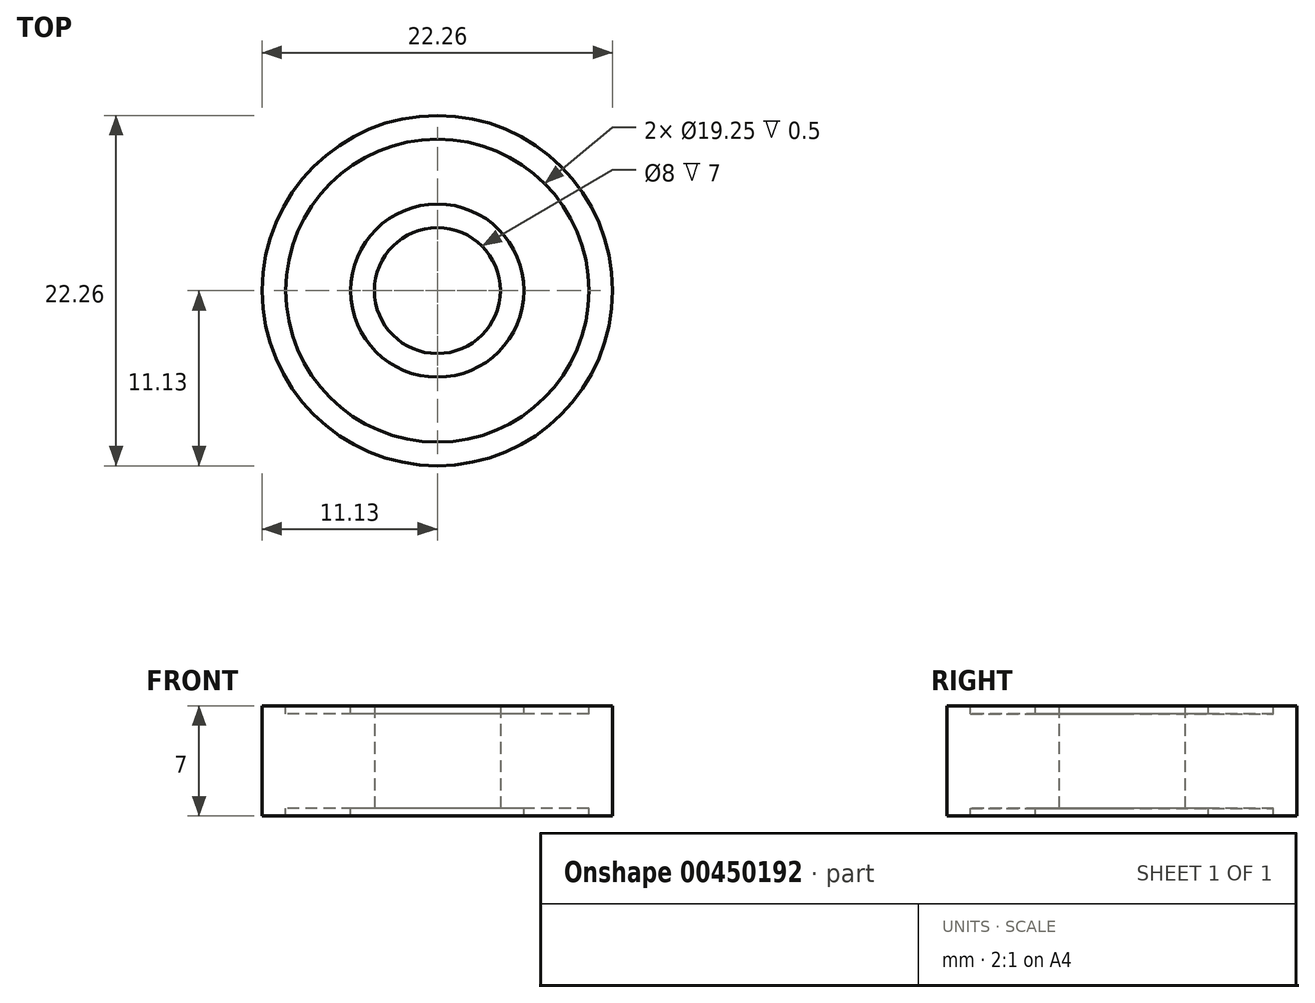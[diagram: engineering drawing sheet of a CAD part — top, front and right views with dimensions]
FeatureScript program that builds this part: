
annotation { "Feature Type Name" : "Feature", "Feature Type Description" : "" }
export const myFeature = defineFeature(function(context is Context, id is Id, definition is map)
    precondition{}
    {
        {
            var Q0;
            Q0=qCreatedBy(makeId("Top.planeOp"),FACE);
            var sketch = newSketch(context, id + "F0", { "sketchPlane" : qUnion([Q0])});
            skCircle(sketch, "E0", {"center": v(0, 0) * mm, "radius": 11.13 * mm});
            skCircle(sketch, "E1", {"center": v(0, 0) * mm, "radius": 4 * mm});
            skSolve(sketch);
        }
        {
            var Q0;
            Q0=qSketchRegion(id+"F0",true);
            extrude(context, id + "F1", {"entities" : qUnion([Q0]), "endBound" : BoundingType.SYMMETRIC, "depth" : 7 * mm, "offsetDistance" : 25 * mm});
        }
        {
            var Q0;
            Q0=qCreatedBy(makeId("Top.planeOp"),FACE);
            var sketch = newSketch(context, id + "F2", { "sketchPlane" : qUnion([Q0])});
            skCircle(sketch, "E2", {"center": v(0, 0) * mm, "radius": 5.5 * mm});
            skCircle(sketch, "E3", {"center": v(0, 0) * mm, "radius": 9.63 * mm});
            skSolve(sketch);
        }
        {
            var Q0;
            Q0=qSketchRegion(id+"F2",true);
            extrude(context, id + "F3", {"entities" : qUnion([Q0]), "operationType" : NewBodyOperationType.REMOVE, "endBound" : BoundingType.SYMMETRIC, "oppositeDirection" : true, "depth" : 25 * mm, "offsetDistance" : 25 * mm});
        }
        {
            var Q0;
            Q0=qSketchRegion(id+"F2",true);
            extrude(context, id + "F4", {"entities" : qUnion([Q0]), "operationType" : NewBodyOperationType.ADD, "endBound" : BoundingType.SYMMETRIC, "depth" : 6 * mm, "offsetDistance" : 25 * mm});
        }
    });
